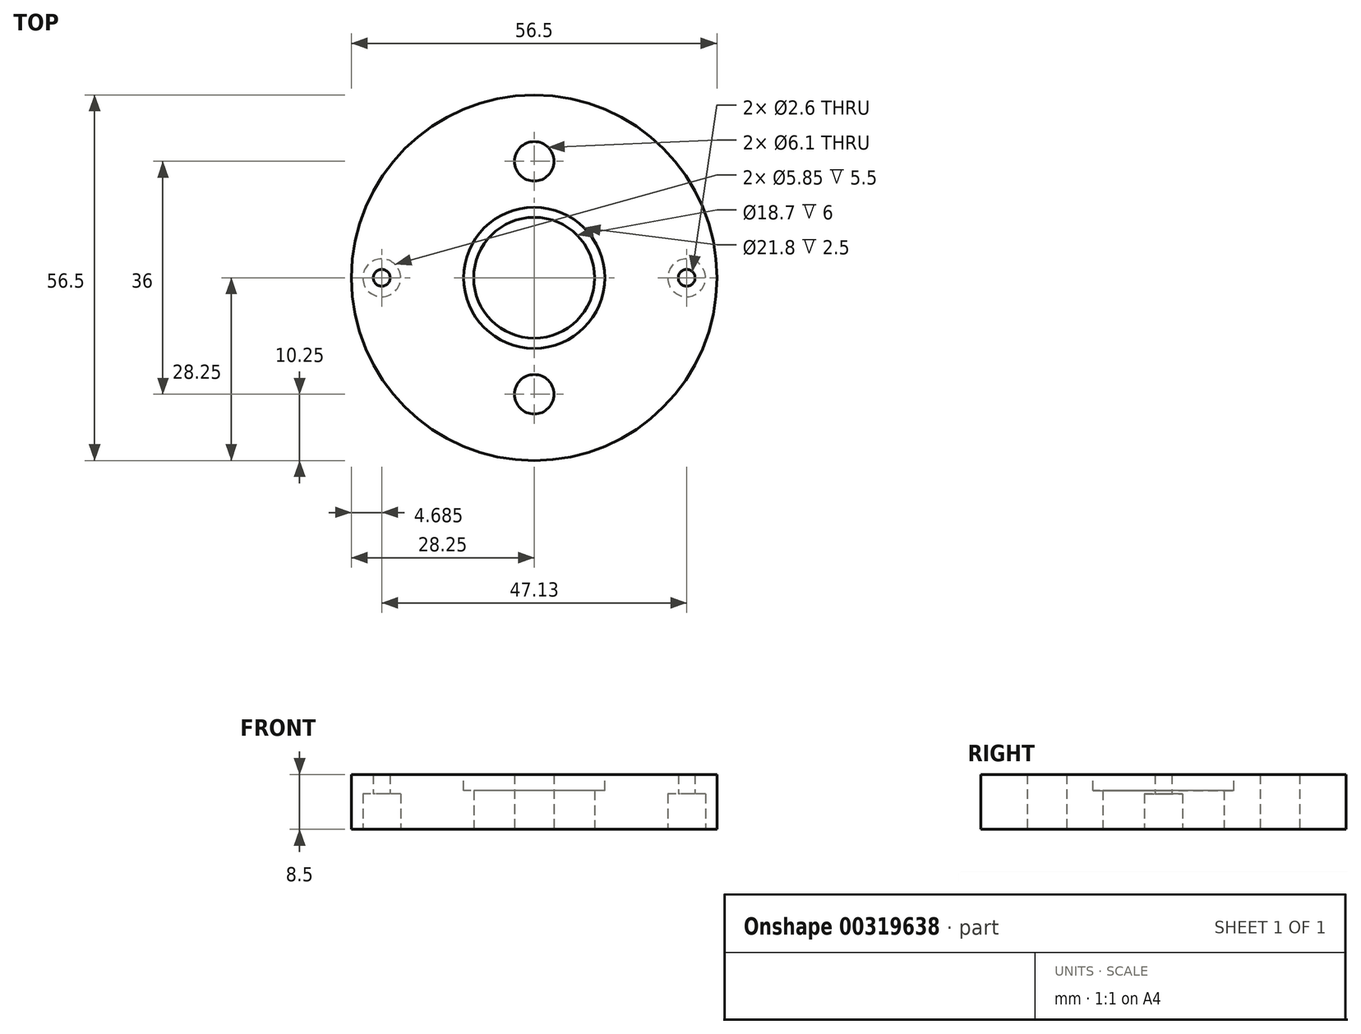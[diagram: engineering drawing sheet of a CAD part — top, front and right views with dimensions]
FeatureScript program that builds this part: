
annotation { "Feature Type Name" : "Feature", "Feature Type Description" : "" }
export const myFeature = defineFeature(function(context is Context, id is Id, definition is map)
    precondition{}
    {
        {
            var Q0;
            Q0=qCreatedBy(makeId("Top.planeOp"),FACE);
            var sketch = newSketch(context, id + "F0", { "sketchPlane" : qUnion([Q0])});
            skCircle(sketch, "E0", {"center": v(0, 0) * mm, "radius": 28.25 * mm});
            skCircle(sketch, "E1", {"center": v(0, 0) * mm, "radius": 9.35 * mm});
            skCircle(sketch, "E2", {"center": v(0, 0) * mm, "radius": 18 * mm, "construction": true});
            skLineSegment(sketch, "E3", {"start": v(0, 28.25) * mm, "end": v(0, -28.25) * mm, "construction": true});
            skCircle(sketch, "E4", {"center": v(0, 18) * mm, "radius": 3.05 * mm});
            skCircle(sketch, "E5", {"center": v(0, -18) * mm, "radius": 3.05 * mm});
            skCircle(sketch, "E6", {"center": v(0, 0) * mm, "radius": 23.57 * mm, "construction": true});
            skLineSegment(sketch, "E7", {"start": v(-28.25, 0) * mm, "end": v(28.25, 0) * mm, "construction": true});
            skCircle(sketch, "E8", {"center": v(-23.57, 0) * mm, "radius": 1.3 * mm});
            skCircle(sketch, "E9", {"center": v(23.57, 0) * mm, "radius": 1.3 * mm});
            skCircle(sketch, "E10", {"center": v(23.57, 0) * mm, "radius": 2.93 * mm});
            skCircle(sketch, "E11", {"center": v(-23.57, 0) * mm, "radius": 2.93 * mm});
            skSolve(sketch);
        }
        {
            var Q0;
            Q0=makeQuery(id+"F0.imprint","IMPRINT",FACE,{"disambiguationData":[TD([[makeQuery(id+"F0.imprint","IMPRINT",EDGE,{"derivedFrom":sQuery(id+"F0.wireOp",EDGE,"E0")}),1.0]])]});
            var Q1;
            Q1=makeQuery(id+"F0.imprint","IMPRINT",FACE,{"disambiguationData":[TD([[makeQuery(id+"F0.imprint","IMPRINT",EDGE,{"derivedFrom":sQuery(id+"F0.wireOp",EDGE,"E9")}),-1.0]])]});
            var Q2;
            Q2=makeQuery(id+"F0.imprint","IMPRINT",FACE,{"disambiguationData":[TD([[makeQuery(id+"F0.imprint","IMPRINT",EDGE,{"derivedFrom":sQuery(id+"F0.wireOp",EDGE,"E8")}),-1.0]])]});
            extrude(context, id + "F1", {"entities" : qUnion([Q0, Q1, Q2]), "flatOperationType" : FlatOperationType.REMOVE, "offsetDistance" : 25 * mm, "depth" : 8.5 * mm, "domain" : OperationDomain.MODEL});
        }
        {
            var Q0;
            Q0=makeQuery(id+"F0.imprint","IMPRINT",FACE,{"disambiguationData":[TD([[makeQuery(id+"F0.imprint","IMPRINT",EDGE,{"derivedFrom":sQuery(id+"F0.wireOp",EDGE,"E8")}),-1.0]])]});
            var Q1;
            Q1=makeQuery(id+"F0.imprint","IMPRINT",FACE,{"disambiguationData":[TD([[makeQuery(id+"F0.imprint","IMPRINT",EDGE,{"derivedFrom":sQuery(id+"F0.wireOp",EDGE,"E9")}),-1.0]])]});
            extrude(context, id + "F2", {"entities" : qUnion([Q0, Q1]), "operationType" : NewBodyOperationType.REMOVE, "depth" : 5.5 * mm});
        }
        {
            var Q0;
            Q0=makeQuery(id+"F1.opExtrude","CAP_FACE",FACE,{"disambiguationData":[OSD([sQuery(id+"F0.wireOp",EDGE,"E0"),sQuery(id+"F0.wireOp",EDGE,"E1"),sQuery(id+"F0.wireOp",EDGE,"E4"),sQuery(id+"F0.wireOp",EDGE,"E5"),sQuery(id+"F0.wireOp",EDGE,"E8"),sQuery(id+"F0.wireOp",EDGE,"E9")])],"isStart":false});
            var sketch = newSketch(context, id + "F3", { "sketchPlane" : qUnion([Q0])});
            skPoint(sketch, "E12.0", {"position": v(0, -18) * mm});
            skPoint(sketch, "E13.0", {"position": v(0, 18) * mm});
            skCircle(sketch, "E14.cCircle", {"center": v(0, -18) * mm, "radius": 3.7 * mm, "construction": true});
            skLineSegment(sketch, "E14.0", {"start": v(-3.7, -20.14) * mm, "end": v(-3.7, -15.86) * mm});
            skLineSegment(sketch, "E14.1", {"start": v(-3.7, -15.86) * mm, "end": v(0, -13.73) * mm});
            skLineSegment(sketch, "E14.2", {"start": v(0, -13.73) * mm, "end": v(3.7, -15.86) * mm});
            skLineSegment(sketch, "E14.3", {"start": v(3.7, -15.86) * mm, "end": v(3.7, -20.14) * mm});
            skLineSegment(sketch, "E14.4", {"start": v(3.7, -20.14) * mm, "end": v(0, -22.27) * mm});
            skLineSegment(sketch, "E14.5", {"start": v(0, -22.27) * mm, "end": v(-3.7, -20.14) * mm});
            skPoint(sketch, "E14.0.midPoint", {"position": v(-3.7, -18) * mm});
            skCircle(sketch, "E15.cCircle", {"center": v(0, 18) * mm, "radius": 3.7 * mm, "construction": true});
            skLineSegment(sketch, "E15.0", {"start": v(-4.2, 17.25) * mm, "end": v(-2.75, 21.27) * mm});
            skLineSegment(sketch, "E15.1", {"start": v(-2.75, 21.27) * mm, "end": v(1.46, 22.02) * mm});
            skLineSegment(sketch, "E15.2", {"start": v(1.46, 22.02) * mm, "end": v(4.2, 18.75) * mm});
            skLineSegment(sketch, "E15.3", {"start": v(4.2, 18.75) * mm, "end": v(2.75, 14.73) * mm});
            skLineSegment(sketch, "E15.4", {"start": v(2.75, 14.73) * mm, "end": v(-1.46, 13.98) * mm});
            skLineSegment(sketch, "E15.5", {"start": v(-1.46, 13.98) * mm, "end": v(-4.2, 17.25) * mm});
            skPoint(sketch, "E15.0.midPoint", {"position": v(-3.48, 19.26) * mm});
            skPoint(sketch, "E16.0", {"position": v(0, 0) * mm});
            skCircle(sketch, "E17", {"center": v(0, 0) * mm, "radius": 10.9 * mm});
            skSolve(sketch);
        }
        {
            var Q0;
            Q0=makeQuery(id+"F3.imprint","IMPRINT",FACE,{"disambiguationData":[TD([[makeQuery(id+"F3.imprint","IMPRINT",EDGE,{"derivedFrom":sQuery(id+"F3.wireOp",EDGE,"E17")}),1.0]])]});
            extrude(context, id + "F4", {"entities" : qUnion([Q0]), "operationType" : NewBodyOperationType.REMOVE, "oppositeDirection" : true, "depth" : 2.5 * mm});
        }
    });
